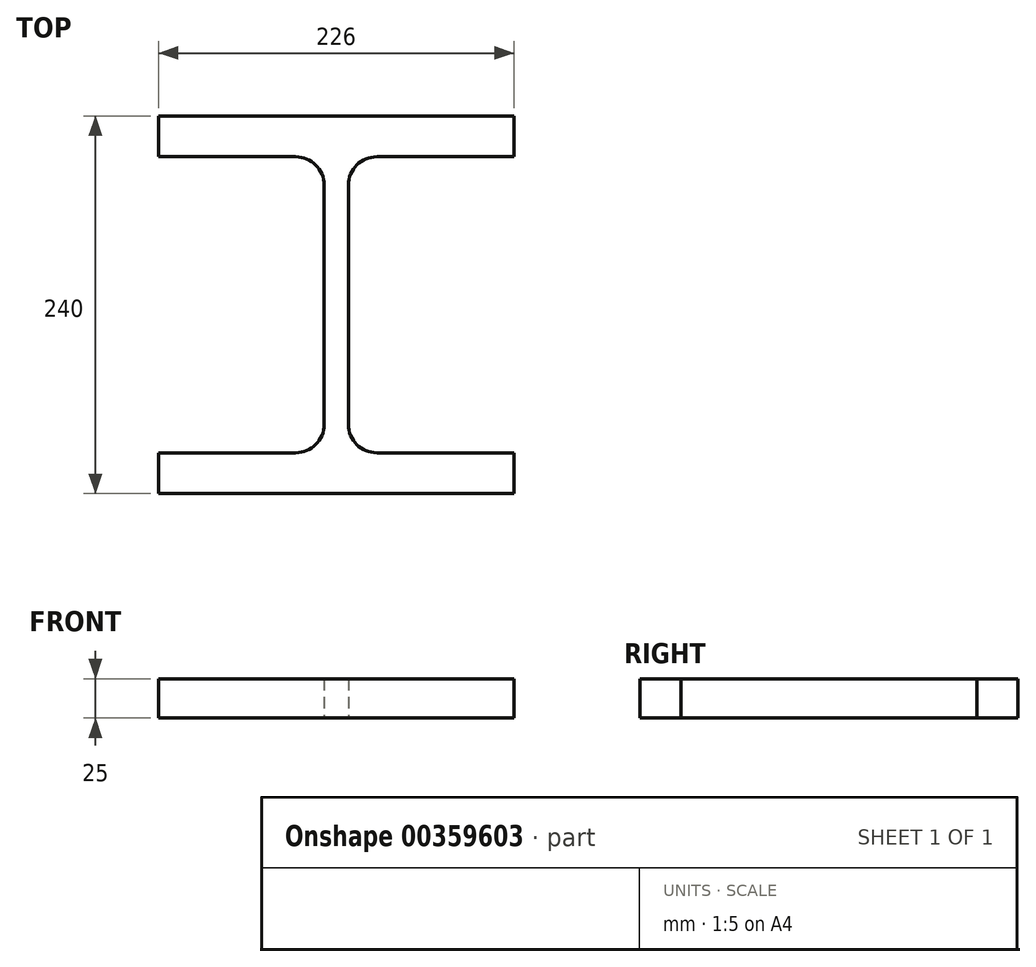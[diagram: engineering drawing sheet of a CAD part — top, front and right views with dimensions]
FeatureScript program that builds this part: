
annotation { "Feature Type Name" : "Feature", "Feature Type Description" : "" }
export const myFeature = defineFeature(function(context is Context, id is Id, definition is map)
    precondition{}
    {
        {
            var Q0;
            Q0=qCreatedBy(makeId("Top.planeOp"),FACE);
            var sketch = newSketch(context, id + "F0", { "sketchPlane" : qUnion([Q0])});
            skLineSegment(sketch, "E0", {"start": v(-120.75, 102.92) * mm, "end": v(105.25, 102.92) * mm});
            skLineSegment(sketch, "E1", {"start": v(-120.75, 102.92) * mm, "end": v(-120.75, 76.92) * mm});
            skLineSegment(sketch, "E2", {"start": v(105.25, 102.92) * mm, "end": v(105.25, 76.92) * mm});
            skLineSegment(sketch, "E3", {"start": v(-120.75, 76.92) * mm, "end": v(-33.5, 76.92) * mm});
            skLineSegment(sketch, "E4", {"start": v(105.25, 76.92) * mm, "end": v(18, 76.92) * mm});
            skLineSegment(sketch, "E5", {"start": v(-15.5, 58.92) * mm, "end": v(-15.5, -93.08) * mm});
            skLineSegment(sketch, "E6", {"start": v(0, 58.92) * mm, "end": v(0, -93.08) * mm});
            skPoint(sketch, "E7.visualSharp", {"position": v(-15.5, 76.92) * mm});
            skArc(sketch, "E7.filletArc", {"start": v(-15.5, 58.92) * mm, "mid": v(-20.77, 71.64) * mm, "end": v(-33.5, 76.92) * mm});
            skPoint(sketch, "E8.visualSharp", {"position": v(0, 76.92) * mm});
            skArc(sketch, "E8.filletArc", {"start": v(18, 76.92) * mm, "mid": v(5.27, 71.64) * mm, "end": v(0, 58.92) * mm});
            skLineSegment(sketch, "E9", {"start": v(-33.5, -111.08) * mm, "end": v(-120.75, -111.08) * mm});
            skLineSegment(sketch, "E10", {"start": v(-120.75, -111.08) * mm, "end": v(-120.75, -137.08) * mm});
            skLineSegment(sketch, "E11", {"start": v(-120.75, -137.08) * mm, "end": v(105.25, -137.08) * mm});
            skLineSegment(sketch, "E12", {"start": v(105.25, -137.08) * mm, "end": v(105.25, -111.08) * mm});
            skLineSegment(sketch, "E13", {"start": v(105.25, -111.08) * mm, "end": v(18, -111.08) * mm});
            skPoint(sketch, "E14.visualSharp", {"position": v(-15.5, -111.08) * mm});
            skArc(sketch, "E14.filletArc", {"start": v(-33.5, -111.08) * mm, "mid": v(-20.77, -105.81) * mm, "end": v(-15.5, -93.08) * mm});
            skPoint(sketch, "E15.visualSharp", {"position": v(0, -111.08) * mm});
            skArc(sketch, "E15.filletArc", {"start": v(0, -93.08) * mm, "mid": v(5.27, -105.81) * mm, "end": v(18, -111.08) * mm});
            skSolve(sketch);
        }
        {
            var Q0;
            Q0 = qSketchRegion(id + "F0", true);
            extrude(context, id + "F1", {"entities" : qUnion([Q0]), "depth" : 25 * mm});
        }
    });
